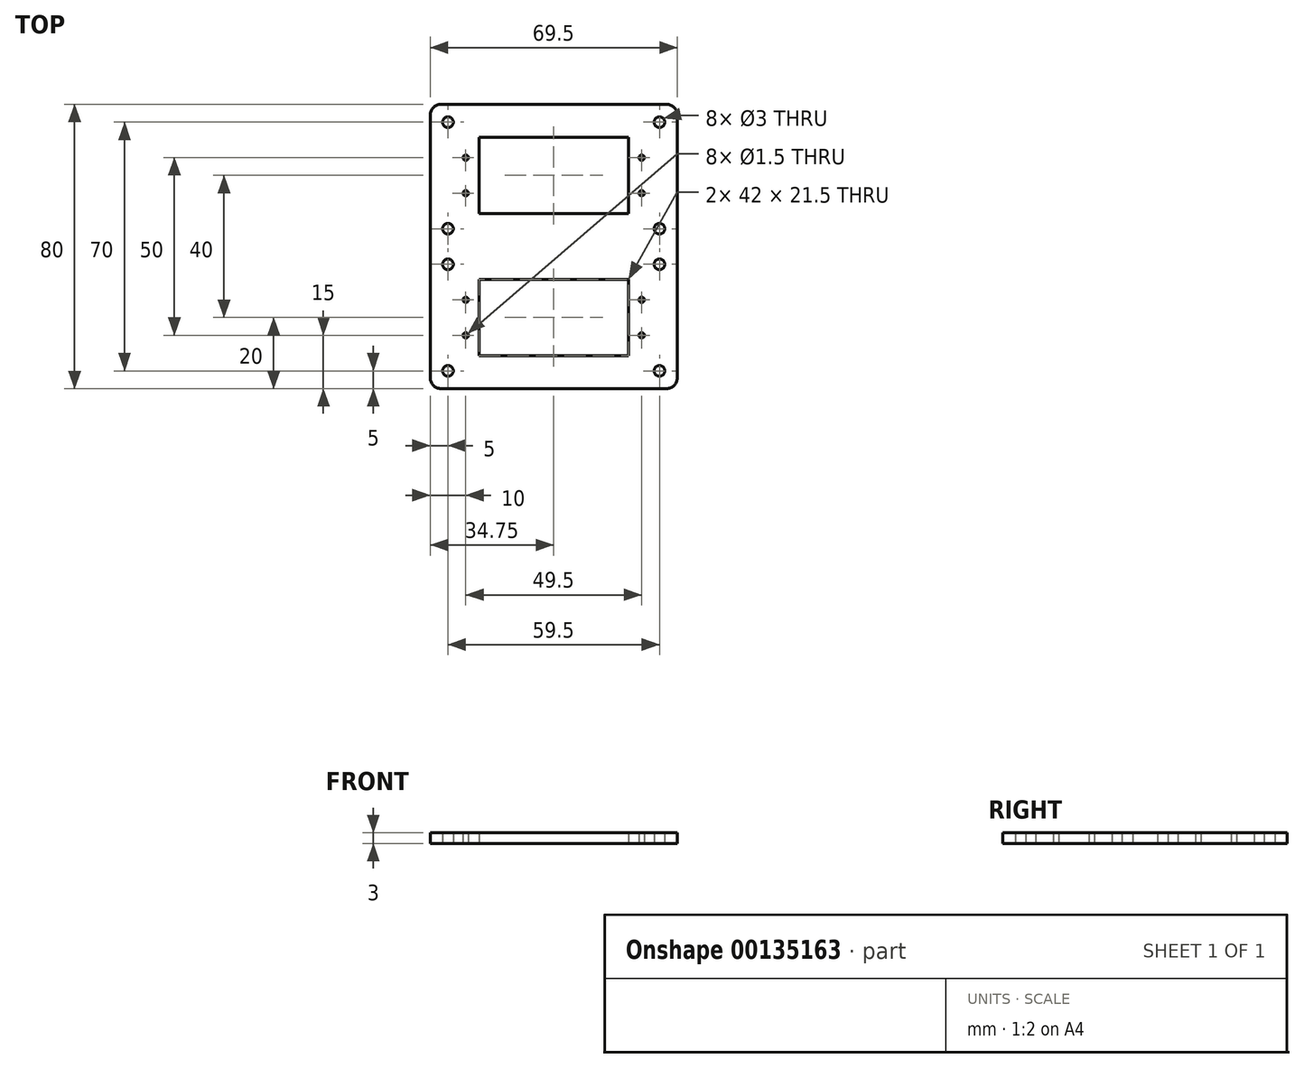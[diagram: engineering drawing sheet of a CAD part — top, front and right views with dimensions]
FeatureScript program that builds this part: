
annotation { "Feature Type Name" : "Feature", "Feature Type Description" : "" }
export const myFeature = defineFeature(function(context is Context, id is Id, definition is map)
    precondition{}
    {
        {
            var Q0;
            Q0=qCreatedBy(makeId("Top.planeOp"),FACE);
            var sketch = newSketch(context, id + "F0", { "sketchPlane" : qUnion([Q0])});
            skLineSegment(sketch, "E0.bottom", {"start": v(21, -10.75) * mm, "end": v(-21, -10.75) * mm});
            skLineSegment(sketch, "E0.top", {"start": v(21, 10.75) * mm, "end": v(-21, 10.75) * mm});
            skLineSegment(sketch, "E0.left", {"start": v(21, -10.75) * mm, "end": v(21, 10.75) * mm});
            skLineSegment(sketch, "E0.right", {"start": v(-21, -10.75) * mm, "end": v(-21, 10.75) * mm});
            skPoint(sketch, "E0.middle", {"position": v(0, 0) * mm});
            skLineSegment(sketch, "E1.bottom", {"start": v(24.75, -5) * mm, "end": v(-24.75, -5) * mm, "construction": true});
            skLineSegment(sketch, "E1.top", {"start": v(24.75, 5) * mm, "end": v(-24.75, 5) * mm, "construction": true});
            skLineSegment(sketch, "E1.left", {"start": v(24.75, -5) * mm, "end": v(24.75, 5) * mm, "construction": true});
            skLineSegment(sketch, "E1.right", {"start": v(-24.75, -5) * mm, "end": v(-24.75, 5) * mm, "construction": true});
            skLineSegment(sketch, "E2.bottom", {"start": v(34.75, -20) * mm, "end": v(-34.75, -20) * mm});
            skLineSegment(sketch, "E2.top", {"start": v(34.75, 20) * mm, "end": v(-34.75, 20) * mm});
            skLineSegment(sketch, "E2.left", {"start": v(34.75, -20) * mm, "end": v(34.75, 20) * mm});
            skLineSegment(sketch, "E2.right", {"start": v(-34.75, -20) * mm, "end": v(-34.75, 20) * mm});
            skLineSegment(sketch, "E3.bottom", {"start": v(-34.75, 20) * mm, "end": v(-29.75, 20) * mm, "construction": true});
            skLineSegment(sketch, "E3.top", {"start": v(-34.75, 15) * mm, "end": v(-29.75, 15) * mm, "construction": true});
            skLineSegment(sketch, "E3.left", {"start": v(-34.75, 20) * mm, "end": v(-34.75, 15) * mm, "construction": true});
            skLineSegment(sketch, "E3.right", {"start": v(-29.75, 20) * mm, "end": v(-29.75, 15) * mm, "construction": true});
            skLineSegment(sketch, "E4.bottom", {"start": v(34.75, 20) * mm, "end": v(29.75, 20) * mm, "construction": true});
            skLineSegment(sketch, "E4.top", {"start": v(34.75, 15) * mm, "end": v(29.75, 15) * mm, "construction": true});
            skLineSegment(sketch, "E4.left", {"start": v(34.75, 20) * mm, "end": v(34.75, 15) * mm, "construction": true});
            skLineSegment(sketch, "E4.right", {"start": v(29.75, 20) * mm, "end": v(29.75, 15) * mm, "construction": true});
            skLineSegment(sketch, "E5.bottom", {"start": v(-34.75, -20) * mm, "end": v(-29.75, -20) * mm, "construction": true});
            skLineSegment(sketch, "E5.top", {"start": v(-34.75, -15) * mm, "end": v(-29.75, -15) * mm, "construction": true});
            skLineSegment(sketch, "E5.left", {"start": v(-34.75, -20) * mm, "end": v(-34.75, -15) * mm, "construction": true});
            skLineSegment(sketch, "E5.right", {"start": v(-29.75, -20) * mm, "end": v(-29.75, -15) * mm, "construction": true});
            skLineSegment(sketch, "E6.bottom", {"start": v(34.75, -20) * mm, "end": v(29.75, -20) * mm, "construction": true});
            skLineSegment(sketch, "E6.top", {"start": v(34.75, -15) * mm, "end": v(29.75, -15) * mm, "construction": true});
            skLineSegment(sketch, "E6.left", {"start": v(34.75, -20) * mm, "end": v(34.75, -15) * mm, "construction": true});
            skLineSegment(sketch, "E6.right", {"start": v(29.75, -20) * mm, "end": v(29.75, -15) * mm, "construction": true});
            skCircle(sketch, "E7", {"center": v(-29.75, 15) * mm, "radius": 1.5 * mm});
            skCircle(sketch, "E8", {"center": v(29.75, 15) * mm, "radius": 1.5 * mm});
            skCircle(sketch, "E9", {"center": v(-29.75, -15) * mm, "radius": 1.5 * mm});
            skCircle(sketch, "E10", {"center": v(29.75, -15) * mm, "radius": 1.5 * mm});
            skCircle(sketch, "E11", {"center": v(-24.75, 5) * mm, "radius": 0.75 * mm});
            skCircle(sketch, "E12", {"center": v(24.75, 5) * mm, "radius": 0.75 * mm});
            skCircle(sketch, "E13", {"center": v(-24.75, -5) * mm, "radius": 0.75 * mm});
            skCircle(sketch, "E14", {"center": v(24.75, -5) * mm, "radius": 0.75 * mm});
            skSolve(sketch);
        }
        {
            var Q0;
            Q0=makeQuery(id+"F0.imprint","IMPRINT",FACE,{"disambiguationData":[TD([[makeQuery(id+"F0.imprint","IMPRINT",EDGE,{"derivedFrom":sQuery(id+"F0.wireOp",EDGE,"E0.bottom")}),1.0]])]});
            extrude(context, id + "F1", {"entities" : qUnion([Q0]), "depth" : 3 * mm});
        }
        {
            var Q0;
            Q0=makeQuery(id+"F1.opExtrude","SWEPT_BODY",BODY,{"disambiguationData":[OSD([sQuery(id+"F0.wireOp",EDGE,"E0.bottom"),sQuery(id+"F0.wireOp",EDGE,"E0.top"),sQuery(id+"F0.wireOp",EDGE,"E0.left"),sQuery(id+"F0.wireOp",EDGE,"E0.right"),sQuery(id+"F0.wireOp",EDGE,"E2.bottom"),sQuery(id+"F0.wireOp",EDGE,"E2.top"),sQuery(id+"F0.wireOp",EDGE,"E2.left"),sQuery(id+"F0.wireOp",EDGE,"E2.right"),sQuery(id+"F0.wireOp",EDGE,"E7"),sQuery(id+"F0.wireOp",EDGE,"E8"),sQuery(id+"F0.wireOp",EDGE,"E9"),sQuery(id+"F0.wireOp",EDGE,"E10"),sQuery(id+"F0.wireOp",EDGE,"E11"),sQuery(id+"F0.wireOp",EDGE,"E12"),sQuery(id+"F0.wireOp",EDGE,"E13"),sQuery(id+"F0.wireOp",EDGE,"E14")])]});
            var Q1;
            Q1=makeQuery(id+"F1.opExtrude","SWEPT_FACE",FACE,{"disambiguationData":[OSD([sQuery(id+"F0.wireOp",EDGE,"E2.bottom")])]});
            mirror(context, id + "F2", {"operationType" : NewBodyOperationType.ADD, "entities" : qUnion([Q0]), "mirrorPlane" : qUnion([Q1])});
        }
        {
            var Q0;
            Q0=makeQuery(id+"F2.opPattern","COPY",EDGE,{"derivedFrom":makeQuery(id+"F1.opExtrude","SWEPT_EDGE",EDGE,{"disambiguationData":[OSD([sQuery(id+"F0.wireOp",EDGE,"E2.top"),sQuery(id+"F0.wireOp",EDGE,"E2.right")])]}),"instanceName":"1"});
            var Q1;
            Q1=makeQuery(id+"F2.opPattern","COPY",EDGE,{"derivedFrom":makeQuery(id+"F1.opExtrude","SWEPT_EDGE",EDGE,{"disambiguationData":[OSD([sQuery(id+"F0.wireOp",EDGE,"E2.top"),sQuery(id+"F0.wireOp",EDGE,"E2.left")])]}),"instanceName":"1"});
            var Q2;
            Q2=makeQuery(id+"F1.opExtrude","SWEPT_EDGE",EDGE,{"disambiguationData":[OSD([sQuery(id+"F0.wireOp",EDGE,"E2.top"),sQuery(id+"F0.wireOp",EDGE,"E2.left")])]});
            var Q3;
            Q3=makeQuery(id+"F1.opExtrude","SWEPT_EDGE",EDGE,{"disambiguationData":[OSD([sQuery(id+"F0.wireOp",EDGE,"E2.top"),sQuery(id+"F0.wireOp",EDGE,"E2.right")])]});
            fillet(context, id + "F3", {"entities" : qUnion([Q0, Q1, Q2, Q3]), "radius" : 3 * mm, "tangentPropagation" : true, "allowEdgeOverflow" : false});
        }
    });
